# Revit family: Mailboxes_Cluster_Box_Units-Salsbury_Industries-Type_I_II_III_IV
name_source: partatom
category: Specialty Equipment
revit_build: Autodesk Revit 2016 (Build: 20150714_1515(x64)
units: mm (PartAtom-declared; Revit-internal decimal feet)

## family parameters
Always vertical = Yes
Cut with Voids When Loaded = No
OmniClass Number = 23.40.90.14.11
OmniClass Title = Mail Boxes
Part Type = Normal
Room Calculation Point = No
Round Connector Dimension = Use Diameter
Shared = No
Work Plane-Based = Yes

## types (4) — shared parameters
Assembly Code = E1010900
Assembly Description = Other Commercial Equipment
Depth = 17.97 "
Height = 62.045 "
Lock Material = Stainless Steel - Salsbury Finish -  Polished
Manufacturer = Salsbury Industries
MasterFormat Number = 10 55 00
MasterFormat Title = Postal Specialties
OmniClass 23 Number = 23.40.90.14.11
OmniClass 23 Title = Mail Boxes
Type Comments = Cluster Box Unit (CBU) - Includes Pedestal
URL = www.mailboxes.com
Version = 2.0 (06/30/17)
Width = 30.51 "

## per-type parameters (varying)
- 3316: Box Height=48.025 "; Description=16 A Doors, 1 Large Parcel Locker, 1 Small Parcel Locker - Type III - USPS Access; Door Slot L1=3300 Series CBU Door Configurations : A Door; Door Slot L1B=3300 Series CBU Door Configurations : Empty; Door Slot L2=3300 Series CBU Door Configurations : A Door w/ Divider; Door Slot L2B=3300 Series CBU Door Configurations : Empty; Door Slot L3=3300 Series CBU Door Configurations : A Door w/ Divider; Door Slot L3B=3300 Series CBU Door Configurations : Empty; Door Slot L4=3300 Series CBU Door Configurations : A Door w/ Divider; Door Slot L4B=3300 Series CBU Door Configurations : Empty; Door Slot L5=3300 Series CBU Door Configurations : A Door; Door Slot L5B=3300 Series CBU Door Configurations : Empty; Door Slot L6=3300 Series CBU Door Configurations : A Door w/ Divider; Door Slot L6B=3300 Series CBU Door Configurations : Empty; Door Slot L7=3300 Series CBU Door Configurations : A Door w/ Divider; Door Slot L7B=3300 Series CBU Door Configurations : Empty; Door Slot L8=3300 Series CBU Door Configurations : A Door w/ Divider; Door Slot L9=3300 Series CBU Parcel Configurations : CBU Large Parcel; Door Slot R1=3300 Series CBU Door Configurations : A Door; Door Slot R1B=3300 Series CBU Door Configurations : Empty; Door Slot R2=3300 Series CBU Door Configurations : A Door w/ Divider; Door Slot R2B=3300 Series CBU Door Configurations : Empty; Door Slot R3=3300 Series CBU Door Configurations : A Door w/ Divider; Door Slot R3B=3300 Series CBU Door Configurations : Empty; Door Slot R4=3300 Series CBU Door Configurations : A Door w/ Divider; Door Slot R4B=3300 Series CBU Door Configurations : Empty; Door Slot R5=3300 Series CBU Door Configurations : A Door w/ Divider; Door Slot R5B=3300 Series CBU Door Configurations : Empty; Door Slot R6=3300 Series CBU Door Configurations : A Door w/ Divider; Door Slot R6B=3300 Series CBU Door Configurations : Empty; Door Slot R7=3300 Series CBU Door Configurations : A Door w/ Divider; Door Slot R7B=3300 Series CBU Door Configurations : Empty; Door Slot R8=3300 Series CBU Door Configurations : A Door w/ Divider; Door Slot R9=3300 Series CBU Parcel Configurations : CBU Small Parcel; Pedestal Height=14.5 "; Visible Divider-High=Yes; Visible Divider-Low=No
- 3312: Box Height=34.025 "; Description=12 A Doors, 1 Small Parcel Locker - Type II - USPS Access; Door Slot L1=3300 Series CBU Door Configurations : A Door; Door Slot L1B=3300 Series CBU Door Configurations : Empty; Door Slot L2=3300 Series CBU Door Configurations : A Door w/ Divider; Door Slot L2B=3300 Series CBU Door Configurations : Empty; Door Slot L3=3300 Series CBU Door Configurations : A Door w/ Divider; Door Slot L3B=3300 Series CBU Door Configurations : Empty; Door Slot L4=3300 Series CBU Door Configurations : A Door w/ Divider; Door Slot L4B=3300 Series CBU Door Configurations : Empty; Door Slot L5=3300 Series CBU Door Configurations : A Door; Door Slot L5B=3300 Series CBU Door Configurations : Empty; Door Slot L6=3300 Series CBU Door Configurations : A Door w/ Divider; Door Slot L6B=3300 Series CBU Door Configurations : Empty; Door Slot L7=3300 Series CBU Door Configurations : A Door w/ Divider; Door Slot L7B=3300 Series CBU Door Configurations : Empty; Door Slot L8=3300 Series CBU Door Configurations : A Door w/ Divider; Door Slot L9=3300 Series CBU Door Configurations : Empty; Door Slot R1=3300 Series CBU Door Configurations : A Door; Door Slot R1B=3300 Series CBU Door Configurations : Empty; Door Slot R2=3300 Series CBU Door Configurations : A Door w/ Divider; Door Slot R2B=3300 Series CBU Door Configurations : Empty; Door Slot R3=3300 Series CBU Door Configurations : A Door w/ Divider; Door Slot R3B=3300 Series CBU Door Configurations : Empty; Door Slot R4=3300 Series CBU Door Configurations : A Door w/ Divider; Door Slot R4B=3300 Series CBU Door Configurations : Empty; Door Slot R5=3300 Series CBU Door Configurations : Empty; Door Slot R5B=3300 Series CBU Door Configurations : Empty; Door Slot R6=3300 Series CBU Door Configurations : Empty; Door Slot R6B=3300 Series CBU Door Configurations : Empty; Door Slot R7=3300 Series CBU Door Configurations : Empty; Door Slot R7B=3300 Series CBU Door Configurations : Empty; Door Slot R8=3300 Series CBU Door Configurations : Empty; Door Slot R9=3300 Series CBU Parcel Configurations : CBU Small Parcel; Pedestal Height=28.5 "; Visible Divider-High=Yes; Visible Divider-Low=No
- 3308: Box Height=34.025 "; Description=8 A Doors, 1 Large Parcel Locker, 1 Small Parcel Locker - Type I - USPS Access; Door Slot L1=3300 Series CBU Door Configurations : A Door; Door Slot L1B=3300 Series CBU Door Configurations : Empty; Door Slot L2=3300 Series CBU Door Configurations : A Door w/ Divider; Door Slot L2B=3300 Series CBU Door Configurations : Empty; Door Slot L3=3300 Series CBU Door Configurations : A Door w/ Divider; Door Slot L3B=3300 Series CBU Door Configurations : Empty; Door Slot L4=3300 Series CBU Door Configurations : A Door w/ Divider; Door Slot L4B=3300 Series CBU Door Configurations : Empty; Door Slot L5=3300 Series CBU Door Configurations : Empty; Door Slot L5B=3300 Series CBU Door Configurations : Empty; Door Slot L6=3300 Series CBU Door Configurations : Empty; Door Slot L6B=3300 Series CBU Door Configurations : Empty; Door Slot L7=3300 Series CBU Door Configurations : Empty; Door Slot L7B=3300 Series CBU Door Configurations : Empty; Door Slot L8=3300 Series CBU Door Configurations : Empty; Door Slot L9=3300 Series CBU Parcel Configurations : CBU Large Parcel; Door Slot R1=3300 Series CBU Door Configurations : A Door; Door Slot R1B=3300 Series CBU Door Configurations : Empty; Door Slot R2=3300 Series CBU Door Configurations : A Door w/ Divider; Door Slot R2B=3300 Series CBU Door Configurations : Empty; Door Slot R3=3300 Series CBU Door Configurations : A Door w/ Divider; Door Slot R3B=3300 Series CBU Door Configurations : Empty; Door Slot R4=3300 Series CBU Door Configurations : A Door w/ Divider; Door Slot R4B=3300 Series CBU Door Configurations : Empty; Door Slot R5=3300 Series CBU Door Configurations : Empty; Door Slot R5B=3300 Series CBU Door Configurations : Empty; Door Slot R6=3300 Series CBU Door Configurations : Empty; Door Slot R6B=3300 Series CBU Door Configurations : Empty; Door Slot R7=3300 Series CBU Door Configurations : Empty; Door Slot R7B=3300 Series CBU Door Configurations : Empty; Door Slot R8=3300 Series CBU Door Configurations : Empty; Door Slot R9=3300 Series CBU Parcel Configurations : CBU Small Parcel; Pedestal Height=28.5 "; Visible Divider-High=Yes; Visible Divider-Low=No
- 3313: Box Height=48.025 "; Description=13 B Doors, 1 Small Parcel Locker - Type IV - USPS Access; Door Slot L1=3300 Series CBU Door Configurations : Empty; Door Slot L1B=3300 Series CBU Door Configurations : B Door; Door Slot L2=3300 Series CBU Door Configurations : Empty; Door Slot L2B=3300 Series CBU Door Configurations : B Door w/ Divider; Door Slot L3=3300 Series CBU Door Configurations : Empty; Door Slot L3B=3300 Series CBU Door Configurations : B Door w/ Divider; Door Slot L4=3300 Series CBU Door Configurations : Empty; Door Slot L4B=3300 Series CBU Door Configurations : B Door w/ Divider; Door Slot L5=3300 Series CBU Door Configurations : Empty; Door Slot L5B=3300 Series CBU Door Configurations : B Door; Door Slot L6=3300 Series CBU Door Configurations : Empty; Door Slot L6B=3300 Series CBU Door Configurations : B Door w/ Divider; Door Slot L7=3300 Series CBU Door Configurations : Empty; Door Slot L7B=3300 Series CBU Parcel Configurations : CBU Small Parcel; Door Slot L8=3300 Series CBU Door Configurations : Empty; Door Slot L9=3300 Series CBU Door Configurations : Empty; Door Slot R1=3300 Series CBU Door Configurations : Empty; Door Slot R1B=3300 Series CBU Door Configurations : B Door; Door Slot R2=3300 Series CBU Door Configurations : Empty; Door Slot R2B=3300 Series CBU Door Configurations : B Door w/ Divider; Door Slot R3=3300 Series CBU Door Configurations : Empty; Door Slot R3B=3300 Series CBU Door Configurations : B Door w/ Divider; Door Slot R4=3300 Series CBU Door Configurations : Empty; Door Slot R4B=3300 Series CBU Door Configurations : B Door w/ Divider; Door Slot R5=3300 Series CBU Door Configurations : Empty; Door Slot R5B=3300 Series CBU Door Configurations : B Door w/ Divider; Door Slot R6=3300 Series CBU Door Configurations : Empty; Door Slot R6B=3300 Series CBU Door Configurations : B Door w/ Divider; Door Slot R7=3300 Series CBU Door Configurations : Empty; Door Slot R7B=3300 Series CBU Door Configurations : B Door w/ Divider; Door Slot R8=3300 Series CBU Door Configurations : Empty; Door Slot R9=3300 Series CBU Door Configurations : Empty; Pedestal Height=14.5 "; Visible Divider-High=No; Visible Divider-Low=Yes

note: column(s) folded — value = type name in every type: Model

## geometry (parser evidence)
native form markers: Sweep x15
no freeform markers — native parametric forms only
